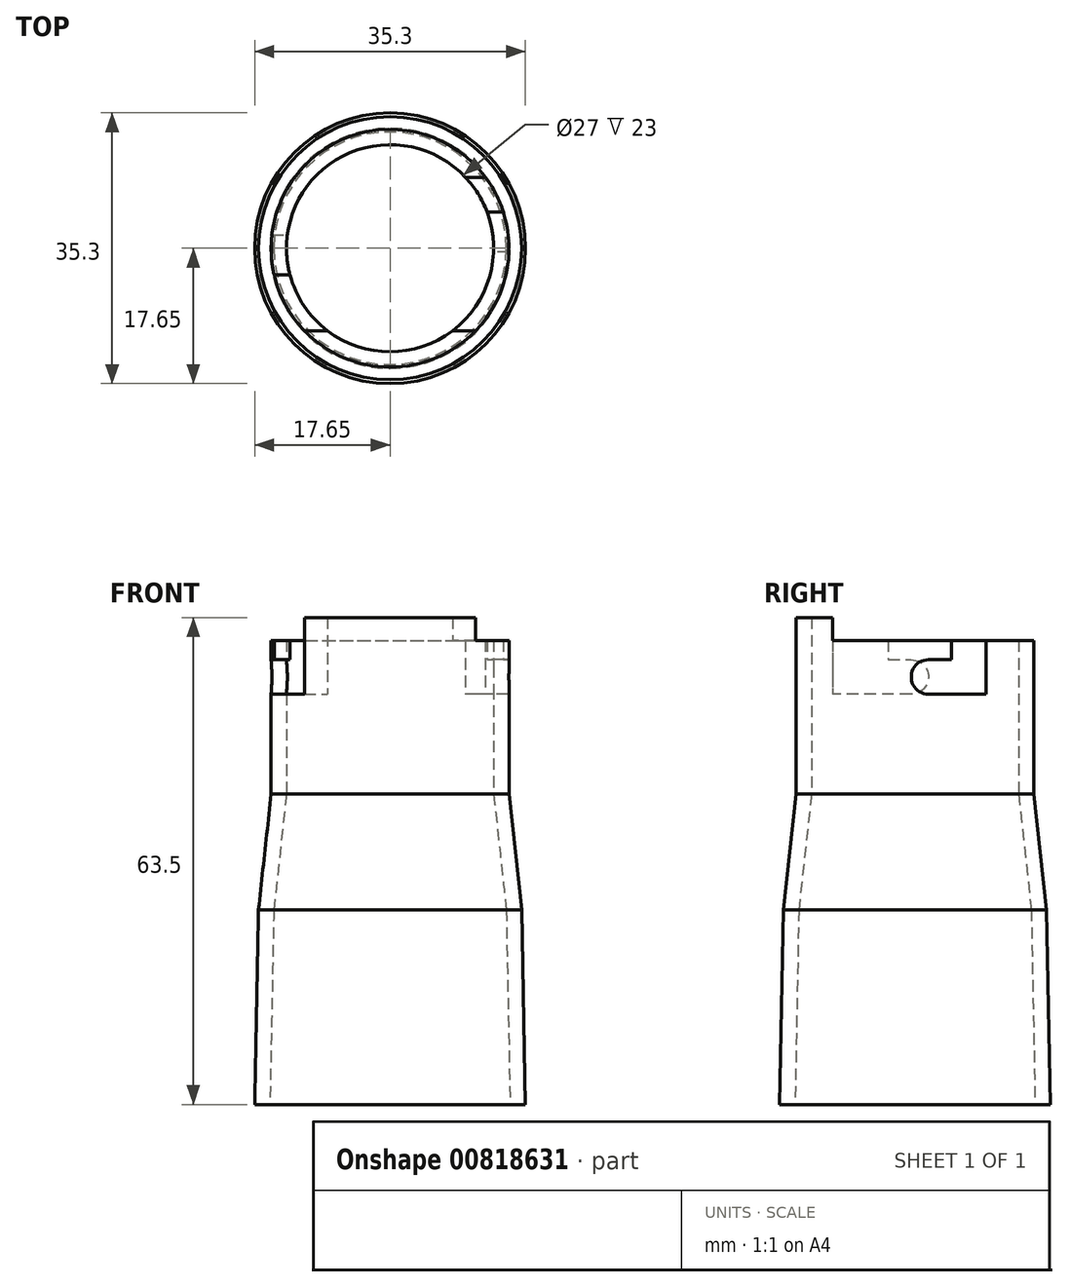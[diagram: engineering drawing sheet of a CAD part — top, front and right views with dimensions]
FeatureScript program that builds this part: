
annotation { "Feature Type Name" : "Feature", "Feature Type Description" : "" }
export const myFeature = defineFeature(function(context is Context, id is Id, definition is map)
    precondition{}
    {
        {
            var Q0;
            Q0=qCreatedBy(makeId("Top.planeOp"),FACE);
            var sketch = newSketch(context, id + "F0", { "sketchPlane" : qUnion([Q0])});
            skCircle(sketch, "E0", {"center": v(0, 0) * mm, "radius": 15.5 * mm});
            skCircle(sketch, "E1.0", {"center": v(0, 0) * mm, "radius": 13.5 * mm});
            skPoint(sketch, "E2", {"position": v(13.5, 0) * mm});
            skPoint(sketch, "E3", {"position": v(0, 13.5) * mm});
            skPoint(sketch, "E4", {"position": v(0, -13.5) * mm});
            skPoint(sketch, "E5", {"position": v(-13.5, 0) * mm});
            skPoint(sketch, "E6", {"position": v(-15.5, 0) * mm});
            skSolve(sketch);
        }
        {
            var Q0;
            Q0=makeQuery(id+"F0.imprint","IMPRINT",FACE,{"disambiguationData":[TD([[makeQuery(id+"F0.imprint","IMPRINT",EDGE,{"derivedFrom":sQuery(id+"F0.wireOp",EDGE,"E0")}),1.0]])]});
            extrude(context, id + "F1", {"entities" : qUnion([Q0]), "depth" : 23 * mm, "offsetDistance" : 25 * mm});
        }
        {
            var Q0;
            Q0=qCreatedBy(makeId("Right.planeOp"),FACE);
            var sketch = newSketch(context, id + "F2", { "sketchPlane" : qUnion([Q0])});
            skLineSegment(sketch, "E7", {"start": v(-10.75, 23) * mm, "end": v(-10.75, 20) * mm});
            skLineSegment(sketch, "E8", {"start": v(-10.75, 20) * mm, "end": v(15.5, 20) * mm});
            skLineSegment(sketch, "E9", {"start": v(15.5, 23) * mm, "end": v(15.5, 0) * mm, "construction": true});
            skLineSegment(sketch, "E10", {"start": v(15.5, 20) * mm, "end": v(15.5, 23) * mm});
            skLineSegment(sketch, "E11.0", {"start": v(-13.5, 23) * mm, "end": v(13.5, 23) * mm, "construction": true});
            skLineSegment(sketch, "E12", {"start": v(-10.75, 23) * mm, "end": v(15.5, 23) * mm});
            skSolve(sketch);
        }
        {
            var Q0;
            Q0 = qSketchRegion(id + "F2", true);
            var Q1;
            Q1=makeQuery(id+"F1.opExtrude","SWEPT_FACE",FACE,{"disambiguationData":[OSD([sQuery(id+"F0.wireOp",EDGE,"E0")])]});
            var Q2;
            Q2=makeQuery(id+"F1.opExtrude","SWEPT_FACE",FACE,{"disambiguationData":[OSD([sQuery(id+"F0.wireOp",EDGE,"E0")])]});
            extrude(context, id + "F3", {"entities" : qUnion([Q0]), "operationType" : NewBodyOperationType.REMOVE, "endBound" : BoundingType.UP_TO_SURFACE, "oppositeDirection" : true, "depth" : 25 * mm, "endBoundEntityFace" : qUnion([Q1]), "offsetDistance" : 25 * mm, "hasSecondDirection" : true, "secondDirectionBound" : SecondDirectionBoundingType.UP_TO_SURFACE, "secondDirectionOppositeDirection" : false, "secondDirectionDepth" : 25 * mm, "secondDirectionBoundEntityFace" : qUnion([Q2])});
        }
        {
            var Q0;
            Q0=qCreatedBy(makeId("Right.planeOp"),FACE);
            var sketch = newSketch(context, id + "F4", { "sketchPlane" : qUnion([Q0])});
            skLineSegment(sketch, "E13", {"start": v(-10.75, 20) * mm, "end": v(-10.75, 13) * mm});
            skLineSegment(sketch, "E14", {"start": v(-10.75, 20) * mm, "end": v(-3.5, 20) * mm});
            skLineSegment(sketch, "E15", {"start": v(-3.5, 20) * mm, "end": v(-3.5, 17.5) * mm});
            skLineSegment(sketch, "E16", {"start": v(-3.5, 17.5) * mm, "end": v(-0.5, 17.5) * mm});
            skLineSegment(sketch, "E17", {"start": v(-0.5, 17.5) * mm, "end": v(-0.5, 13) * mm, "construction": true});
            skLineSegment(sketch, "E18", {"start": v(-0.5, 13) * mm, "end": v(-10.75, 13) * mm});
            skArc(sketch, "E19", {"start": v(-0.5, 17.5) * mm, "mid": v(1.75, 15.25) * mm, "end": v(-0.5, 13) * mm});
            skLineSegment(sketch, "E20.0", {"start": v(-10.75, 20) * mm, "end": v(13.5, 20) * mm, "construction": true});
            skSolve(sketch);
        }
        {
            var Q0;
            Q0=qCreatedBy(makeId("Right.planeOp"),FACE);
            var sketch = newSketch(context, id + "F5", { "sketchPlane" : qUnion([Q0])});
            skLineSegment(sketch, "E21.0", {"start": v(-10.75, 20) * mm, "end": v(15.5, 20) * mm, "construction": true});
            skLineSegment(sketch, "E22", {"start": v(4.75, 17.5) * mm, "end": v(1.75, 17.5) * mm});
            skLineSegment(sketch, "E23", {"start": v(1.75, 17.5) * mm, "end": v(1.75, 13) * mm, "construction": true});
            skLineSegment(sketch, "E24", {"start": v(1.75, 13) * mm, "end": v(9.25, 13) * mm});
            skLineSegment(sketch, "E25", {"start": v(9.25, 20) * mm, "end": v(0, 20) * mm});
            skArc(sketch, "E26", {"start": v(1.75, 17.5) * mm, "mid": v(-0.5, 15.25) * mm, "end": v(1.75, 13) * mm});
            skLineSegment(sketch, "E27", {"start": v(4.75, 17.5) * mm, "end": v(4.75, 20) * mm});
            skLineSegment(sketch, "E28", {"start": v(0, 20) * mm, "end": v(4.75, 20) * mm});
            skLineSegment(sketch, "E29", {"start": v(9.25, 13) * mm, "end": v(9.25, 20) * mm});
            skSolve(sketch);
        }
        {
            var Q0;
            Q0 = qSketchRegion(id + "F4", true);
            var Q1;
            Q1=makeQuery(id+"F1.opExtrude","SWEPT_FACE",FACE,{"disambiguationData":[OSD([sQuery(id+"F0.wireOp",EDGE,"E0")])]});
            extrude(context, id + "F6", {"entities" : qUnion([Q0]), "operationType" : NewBodyOperationType.REMOVE, "endBound" : BoundingType.UP_TO_SURFACE, "oppositeDirection" : true, "depth" : 25 * mm, "endBoundEntityFace" : qUnion([Q1]), "offsetDistance" : 25 * mm});
        }
        {
            var Q0;
            Q0 = qSketchRegion(id + "F5", true);
            var Q1;
            Q1=makeQuery(id+"F1.opExtrude","SWEPT_FACE",FACE,{"disambiguationData":[OSD([sQuery(id+"F0.wireOp",EDGE,"E0")])]});
            extrude(context, id + "F7", {"entities" : qUnion([Q0]), "operationType" : NewBodyOperationType.REMOVE, "endBound" : BoundingType.UP_TO_SURFACE, "depth" : 25 * mm, "endBoundEntityFace" : qUnion([Q1]), "offsetDistance" : 25 * mm});
        }
        {
            var Q0;
            Q0=qCreatedBy(makeId("Top.planeOp"),FACE);
            cPlane(context, id + "F8", {"entities" : qUnion([Q0]), "cplaneType" : CPlaneType.OFFSET, "offset" : 15.1 * mm, "oppositeDirection" : true, "width" : 150 * mm, "height" : 150 * mm});
        }
        {
            var Q0;
            Q0=qCreatedBy(id+"F8.planeOp",FACE);
            var sketch = newSketch(context, id + "F9", { "sketchPlane" : qUnion([Q0])});
            skCircle(sketch, "E30.0", {"center": v(0, 0) * mm, "radius": 17.15 * mm});
            skCircle(sketch, "E31.0", {"center": v(0, 0) * mm, "radius": 15.15 * mm});
            skPoint(sketch, "E32", {"position": v(0, -15.15) * mm});
            skPoint(sketch, "E33", {"position": v(0, 15.15) * mm});
            skPoint(sketch, "E34", {"position": v(15.15, 0) * mm});
            skPoint(sketch, "E35", {"position": v(-15.15, 0) * mm});
            skPoint(sketch, "E36", {"position": v(-17.15, 0) * mm});
            skSolve(sketch);
        }
        {
            var Q0;
            Q0=qCreatedBy(makeId("Front.planeOp"),FACE);
            var sketch = newSketch(context, id + "F10", { "sketchPlane" : qUnion([Q0])});
            skPoint(sketch, "E37.0", {"position": v(-13.5, 0) * mm});
            skPoint(sketch, "E38.0", {"position": v(-15.15, -15.1) * mm});
            skLineSegment(sketch, "E39", {"start": v(-13.5, 0) * mm, "end": v(-15.15, -15.1) * mm});
            skPoint(sketch, "E40.0", {"position": v(-17.15, -15.1) * mm});
            skPoint(sketch, "E41.0", {"position": v(-15.5, 0) * mm});
            skLineSegment(sketch, "E42", {"start": v(-13.5, 0) * mm, "end": v(-15.5, 0) * mm});
            skLineSegment(sketch, "E43", {"start": v(-17.15, -15.1) * mm, "end": v(-15.5, 0) * mm});
            skLineSegment(sketch, "E44", {"start": v(-17.15, -15.1) * mm, "end": v(-15.15, -15.1) * mm});
            skLineSegment(sketch, "E45", {"start": v(0, 2.57) * mm, "end": v(0, -3.65) * mm, "construction": true});
            skSolve(sketch);
        }
        {
            var Q0;
            Q0 = qSketchRegion(id + "F10", true);
            var Q1;
            Q1=sQuery(id+"F10.wireOp",EDGE,"E45");
            revolve(context, id + "F11", {"operationType" : NewBodyOperationType.ADD, "surfaceOperationType" : NewSurfaceOperationType.NEW, "entities" : qUnion([Q0]), "axis" : qUnion([Q1]), "revolveType" : RevolveType.FULL});
        }
        {
            var Q0;
            Q0=qCreatedBy(id+"F8.planeOp",FACE);
            cPlane(context, id + "F12", {"entities" : qUnion([Q0]), "cplaneType" : CPlaneType.OFFSET, "offset" : 25.4 * mm, "oppositeDirection" : true, "width" : 150 * mm, "height" : 150 * mm});
        }
        {
            var Q0;
            Q0=qCreatedBy(id+"F12.planeOp",FACE);
            var sketch = newSketch(context, id + "F13", { "sketchPlane" : qUnion([Q0])});
            skCircle(sketch, "E46.0", {"center": v(0, 0) * mm, "radius": 15.65 * mm});
            skCircle(sketch, "E47.0", {"center": v(0, 0) * mm, "radius": 17.65 * mm});
            skPoint(sketch, "E48", {"position": v(-15.65, 0) * mm});
            skPoint(sketch, "E49", {"position": v(-17.65, 0) * mm});
            skSolve(sketch);
        }
        {
            var Q0;
            Q0=qCreatedBy(makeId("Front.planeOp"),FACE);
            var sketch = newSketch(context, id + "F14", { "sketchPlane" : qUnion([Q0])});
            skPoint(sketch, "E50.0", {"position": v(-17.15, -15.1) * mm});
            skPoint(sketch, "E51.0", {"position": v(-15.15, -15.1) * mm});
            skPoint(sketch, "E52.0", {"position": v(0, -15.1) * mm});
            skPoint(sketch, "E53.0", {"position": v(0, -40.5) * mm});
            skPoint(sketch, "E54.0", {"position": v(-15.65, -40.5) * mm});
            skPoint(sketch, "E55.0", {"position": v(-17.65, -40.5) * mm});
            skLineSegment(sketch, "E56", {"start": v(0, -40.5) * mm, "end": v(0, -15.1) * mm, "construction": true});
            skLineSegment(sketch, "E57", {"start": v(-17.15, -15.1) * mm, "end": v(-17.65, -40.5) * mm});
            skLineSegment(sketch, "E58", {"start": v(-15.65, -40.5) * mm, "end": v(-15.15, -15.1) * mm});
            skLineSegment(sketch, "E59", {"start": v(-15.15, -15.1) * mm, "end": v(-17.15, -15.1) * mm});
            skLineSegment(sketch, "E60", {"start": v(-15.65, -40.5) * mm, "end": v(-17.65, -40.5) * mm});
            skSolve(sketch);
        }
        {
            var Q0;
            Q0 = qSketchRegion(id + "F14", true);
            var Q1;
            Q1=sQuery(id+"F14.wireOp",EDGE,"E56");
            revolve(context, id + "F15", {"operationType" : NewBodyOperationType.ADD, "surfaceOperationType" : NewSurfaceOperationType.NEW, "entities" : qUnion([Q0]), "axis" : qUnion([Q1]), "revolveType" : RevolveType.FULL});
        }
    });
